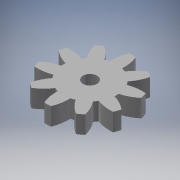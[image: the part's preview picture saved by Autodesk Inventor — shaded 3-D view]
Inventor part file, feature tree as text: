
AUTODESK INVENTOR PART (.ipt)
format: ipt  version: 2018 (Build 220112000, 112)  size: 189,440 bytes
history: native  units: mm (DEFAULTED — no unit token found)
features: plane x3, other x3, sketch x3, extrude x2
ambient origin geometry x8: Origin, YZ Plane, XZ Plane, XY Plane, X Axis, Y Axis, Z Axis, Center Point
bodies: Solid1 (feature_tree)
feature tree (11):
  extrude  "Extrusion1"  Depth=5.0mm TaperAngle=0.0deg
  plane  "Work Plane2"
  plane  "Work Plane8"
  plane  "Work Plane9"
  other  "Stirnzahnrad"
  extrude  "Extrusion2"  Depth=10.0mm TaperAngle=0.0deg
  sketch  "Sketch1"  dims[d0=24.0mm d1=5.0mm d2=0.0mm]
  sketch  "Sketch2"  dims[d3=20.0mm d4=10.0mm d5=0.0mm]
  other  "Srf1"
  sketch  "Skizze3"  dims[d16=20.0mm d17=0.0mm d34=3.141593mm d39=0.0mm d41=0.0mm d43=20.0mm d46=20.0mm d47=0.0mm d48=0.0mm d49=4.0mm d50=10.0mm d51=0.0mm]
  other  "Flankendurchmesser"
